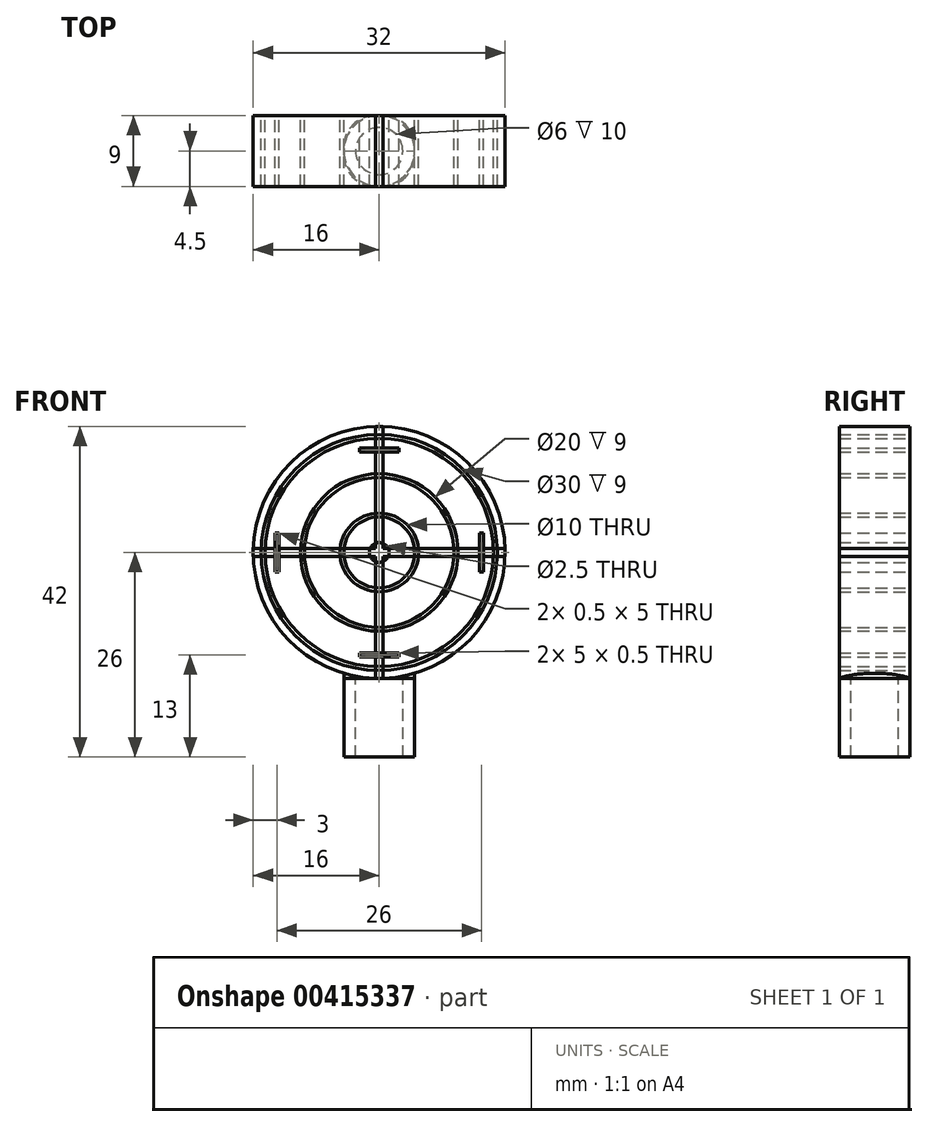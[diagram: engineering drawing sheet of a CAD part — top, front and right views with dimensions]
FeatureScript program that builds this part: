
annotation { "Feature Type Name" : "Feature", "Feature Type Description" : "" }
export const myFeature = defineFeature(function(context is Context, id is Id, definition is map)
    precondition{}
    {
        {
            var Q0;
            Q0=qCreatedBy(makeId("Top.planeOp"),FACE);
            var sketch = newSketch(context, id + "F0", { "sketchPlane" : qUnion([Q0])});
            skCircle(sketch, "E0", {"center": v(0, 0) * mm, "radius": 3 * mm});
            skCircle(sketch, "E1", {"center": v(0, 0) * mm, "radius": 4.5 * mm});
            skSolve(sketch);
        }
        {
            var Q0;
            Q0=makeQuery(id+"F0.imprint","IMPRINT",FACE,{"disambiguationData":[TD([[makeQuery(id+"F0.imprint","IMPRINT",EDGE,{"derivedFrom":sQuery(id+"F0.wireOp",EDGE,"E0")}),-1.0]])]});
            extrude(context, id + "F1", {"entities" : qUnion([Q0]), "oppositeDirection" : true, "depth" : 10 * mm});
        }
        {
            var Q0;
            Q0=qCreatedBy(makeId("Front.planeOp"),FACE);
            var sketch = newSketch(context, id + "F2", { "sketchPlane" : qUnion([Q0])});
            skLineSegment(sketch, "E2", {"start": v(0, 0) * mm, "end": v(0, 16) * mm});
            skCircle(sketch, "E3", {"center": v(0, 16) * mm, "radius": 15 * mm});
            skCircle(sketch, "E4", {"center": v(0, 16) * mm, "radius": 14.5 * mm});
            skCircle(sketch, "E5", {"center": v(0, 16) * mm, "radius": 10 * mm});
            skCircle(sketch, "E6", {"center": v(0, 16) * mm, "radius": 9.5 * mm});
            skCircle(sketch, "E7", {"center": v(0, 16) * mm, "radius": 5 * mm});
            skCircle(sketch, "E8", {"center": v(0, 16) * mm, "radius": 4.5 * mm});
            skCircle(sketch, "E9", {"center": v(0, 16) * mm, "radius": 1.25 * mm});
            skCircle(sketch, "E10", {"center": v(0, 16) * mm, "radius": 0.75 * mm});
            skCircle(sketch, "E11", {"center": v(0, 16) * mm, "radius": 16 * mm});
            skLineSegment(sketch, "E12", {"start": v(0, 0) * mm, "end": v(-4.5, 0) * mm});
            skLineSegment(sketch, "E13", {"start": v(-4.5, 0) * mm, "end": v(-4.5, 0.65) * mm});
            skLineSegment(sketch, "E14", {"start": v(0, 0) * mm, "end": v(4.5, 0) * mm});
            skLineSegment(sketch, "E15", {"start": v(4.5, 0) * mm, "end": v(4.5, 0.65) * mm});
            skSolve(sketch);
        }
        {
            var Q0;
            {var subQ0=sQuery(id+"F2.wireOp",EDGE,"E12");Q0=makeQuery(id+"F2.imprint","IMPRINT",FACE,{"disambiguationData":[TD([[makeQuery(id+"F2.imprint","IMPRINT",EDGE,{"derivedFrom":subQ0}),-1.0]])]});}
            var Q1;
            {var subQ0=sQuery(id+"F2.wireOp",EDGE,"E14");Q1=makeQuery(id+"F2.imprint","IMPRINT",FACE,{"disambiguationData":[TD([[makeQuery(id+"F2.imprint","IMPRINT",EDGE,{"derivedFrom":subQ0}),1.0]])]});}
            var Q2;
            Q2=makeQuery(id+"F2.imprint","IMPRINT",FACE,{"disambiguationData":[TD([[makeQuery(id+"F2.imprint","IMPRINT",EDGE,{"derivedFrom":sQuery(id+"F2.wireOp",EDGE,"E3")}),-1.0]])]});
            var Q3;
            Q3=makeQuery(id+"F2.imprint","IMPRINT",FACE,{"disambiguationData":[TD([[makeQuery(id+"F2.imprint","IMPRINT",EDGE,{"derivedFrom":sQuery(id+"F2.wireOp",EDGE,"E4")}),1.0]])]});
            var Q4;
            Q4=makeQuery(id+"F2.imprint","IMPRINT",FACE,{"disambiguationData":[TD([[makeQuery(id+"F2.imprint","IMPRINT",EDGE,{"derivedFrom":sQuery(id+"F2.wireOp",EDGE,"E6")}),1.0]])]});
            var Q5;
            Q5=makeQuery(id+"F2.imprint","IMPRINT",FACE,{"disambiguationData":[TD([[makeQuery(id+"F2.imprint","IMPRINT",EDGE,{"derivedFrom":sQuery(id+"F2.wireOp",EDGE,"E8")}),1.0]])]});
            extrude(context, id + "F3", {"entities" : qUnion([Q0, Q1, Q2, Q3, Q4, Q5]), "operationType" : NewBodyOperationType.ADD, "endBound" : BoundingType.SYMMETRIC, "depth" : 9 * mm});
        }
        {
            var Q0;
            Q0=makeQuery(id+"F3.opExtrude","CAP_EDGE",EDGE,{"disambiguationData":[OSD([sQuery(id+"F2.wireOp",EDGE,"E13")])],"isStart":false});
            var Q1;
            Q1=makeQuery(id+"F3.opExtrude","CAP_EDGE",EDGE,{"disambiguationData":[OSD([sQuery(id+"F2.wireOp",EDGE,"E15")])],"isStart":false});
            var Q2;
            Q2=makeQuery(id+"F3.opExtrude","CAP_EDGE",EDGE,{"disambiguationData":[OSD([sQuery(id+"F2.wireOp",EDGE,"E15")])],"isStart":true});
            var Q3;
            Q3=makeQuery(id+"F3.opExtrude","CAP_EDGE",EDGE,{"disambiguationData":[OSD([sQuery(id+"F2.wireOp",EDGE,"E13")])],"isStart":true});
            fillet(context, id + "F4", {"entities" : qUnion([Q0, Q1, Q2, Q3]), "radius" : 4 * mm, "tangentPropagation" : true, "allowEdgeOverflow" : false});
        }
        {
            var Q0;
            Q0=makeQuery(id+"F3.opExtrude","CAP_FACE",FACE,{"disambiguationData":[OSD([sQuery(id+"F2.wireOp",EDGE,"E8"),sQuery(id+"F2.wireOp",EDGE,"E9")])],"isStart":true});
            var sketch = newSketch(context, id + "F5", { "sketchPlane" : qUnion([Q0])});
            skLineSegment(sketch, "E16.bottom", {"start": v(0.5, 0) * mm, "end": v(-0.5, 0) * mm});
            skLineSegment(sketch, "E16.top", {"start": v(0.5, 32) * mm, "end": v(-0.5, 32) * mm});
            skLineSegment(sketch, "E16.left", {"start": v(0.5, 0) * mm, "end": v(0.5, 32) * mm});
            skLineSegment(sketch, "E16.right", {"start": v(-0.5, 0) * mm, "end": v(-0.5, 32) * mm});
            skPoint(sketch, "E16.middle", {"position": v(0, 16) * mm});
            skLineSegment(sketch, "E17.bottom", {"start": v(16, 15.5) * mm, "end": v(-16, 15.5) * mm});
            skLineSegment(sketch, "E17.top", {"start": v(16, 16.5) * mm, "end": v(-16, 16.5) * mm});
            skLineSegment(sketch, "E17.left", {"start": v(16, 15.5) * mm, "end": v(16, 16.5) * mm});
            skLineSegment(sketch, "E17.right", {"start": v(-16, 15.5) * mm, "end": v(-16, 16.5) * mm});
            skLineSegment(sketch, "E18", {"start": v(-16, 16) * mm, "end": v(-13, 16) * mm});
            skPoint(sketch, "E18.endSnap0", {"position": v(-16, 16) * mm});
            skLineSegment(sketch, "E19", {"start": v(0, 0) * mm, "end": v(0, 3) * mm});
            skLineSegment(sketch, "E20", {"start": v(16, 16) * mm, "end": v(13, 16) * mm});
            skLineSegment(sketch, "E21", {"start": v(0, 32) * mm, "end": v(0, 29) * mm});
            skLineSegment(sketch, "E22.bottom", {"start": v(-12.75, 13.5) * mm, "end": v(-13.25, 13.5) * mm});
            skLineSegment(sketch, "E22.top", {"start": v(-12.75, 18.5) * mm, "end": v(-13.25, 18.5) * mm});
            skLineSegment(sketch, "E22.left", {"start": v(-12.75, 13.5) * mm, "end": v(-12.75, 18.5) * mm});
            skLineSegment(sketch, "E22.right", {"start": v(-13.25, 13.5) * mm, "end": v(-13.25, 18.5) * mm});
            skPoint(sketch, "E22.middle", {"position": v(-13, 16) * mm});
            skLineSegment(sketch, "E23.bottom", {"start": v(13.25, 13.5) * mm, "end": v(12.75, 13.5) * mm});
            skLineSegment(sketch, "E23.top", {"start": v(13.25, 18.5) * mm, "end": v(12.75, 18.5) * mm});
            skLineSegment(sketch, "E23.left", {"start": v(13.25, 13.5) * mm, "end": v(13.25, 18.5) * mm});
            skLineSegment(sketch, "E23.right", {"start": v(12.75, 13.5) * mm, "end": v(12.75, 18.5) * mm});
            skPoint(sketch, "E23.middle", {"position": v(13, 16) * mm});
            skLineSegment(sketch, "E24.bottom", {"start": v(2.5, 28.75) * mm, "end": v(-2.5, 28.75) * mm});
            skLineSegment(sketch, "E24.top", {"start": v(2.5, 29.25) * mm, "end": v(-2.5, 29.25) * mm});
            skLineSegment(sketch, "E24.left", {"start": v(2.5, 28.75) * mm, "end": v(2.5, 29.25) * mm});
            skLineSegment(sketch, "E24.right", {"start": v(-2.5, 28.75) * mm, "end": v(-2.5, 29.25) * mm});
            skPoint(sketch, "E24.middle", {"position": v(0, 29) * mm});
            skLineSegment(sketch, "E25.bottom", {"start": v(2.5, 2.75) * mm, "end": v(-2.5, 2.75) * mm});
            skLineSegment(sketch, "E25.top", {"start": v(2.5, 3.25) * mm, "end": v(-2.5, 3.25) * mm});
            skLineSegment(sketch, "E25.left", {"start": v(2.5, 2.75) * mm, "end": v(2.5, 3.25) * mm});
            skLineSegment(sketch, "E25.right", {"start": v(-2.5, 2.75) * mm, "end": v(-2.5, 3.25) * mm});
            skPoint(sketch, "E25.middle", {"position": v(0, 3) * mm});
            skSolve(sketch);
        }
        {
            var Q0;
            {var subQ0=sQuery(id+"F5.wireOp",EDGE,"E24.bottom");var subQ1=sQuery(id+"F5.wireOp",EDGE,"E16.left");var subQ2=makeQuery(id+"F5.imprint","INTERSECT",VERTEX,{"derivedFrom":[subQ1,subQ0]});Q0=makeQuery(id+"F5.imprint","IMPRINT",FACE,{"disambiguationData":[TD([[makeQuery(id+"F5.imprint","IMPRINT",EDGE,{"disambiguationData":[TD([[subQ2,1.0]])],"derivedFrom":subQ1}),1.0]])]});}
            var Q1;
            {var subQ0=sQuery(id+"F5.wireOp",EDGE,"E16.right");var subQ1=sQuery(id+"F5.wireOp",EDGE,"E16.top");var subQ2=makeQuery(id+"F5.imprint","INTERSECT",VERTEX,{"derivedFrom":[subQ1,subQ0]});Q1=makeQuery(id+"F5.imprint","IMPRINT",FACE,{"disambiguationData":[TD([[makeQuery(id+"F5.imprint","IMPRINT",EDGE,{"disambiguationData":[TD([[subQ2,1.0]])],"derivedFrom":subQ1}),1.0]])]});}
            var Q2;
            {var subQ0=sQuery(id+"F5.wireOp",EDGE,"E16.left");var subQ1=sQuery(id+"F5.wireOp",EDGE,"E16.top");var subQ2=makeQuery(id+"F5.imprint","INTERSECT",VERTEX,{"derivedFrom":[subQ1,subQ0]});Q2=makeQuery(id+"F5.imprint","IMPRINT",FACE,{"disambiguationData":[TD([[makeQuery(id+"F5.imprint","IMPRINT",EDGE,{"disambiguationData":[TD([[subQ2,-1.0]])],"derivedFrom":subQ1}),1.0]])]});}
            var Q3;
            {var subQ0=sQuery(id+"F5.wireOp",EDGE,"E16.left");var subQ1=makeQuery(id+"F3.opExtrude","CAP_EDGE",EDGE,{"disambiguationData":[OSD([sQuery(id+"F2.wireOp",EDGE,"E8")])],"isStart":true});var subQ2=makeQuery(id+"F5.imprint","INTERSECT",VERTEX,{"disambiguationData":[OD(1.0)],"derivedFrom":[subQ1,subQ0]});Q3=makeQuery(id+"F5.imprint","IMPRINT",FACE,{"disambiguationData":[TD([[makeQuery(id+"F5.imprint","IMPRINT",EDGE,{"disambiguationData":[TD([[subQ2,1.0]])],"derivedFrom":subQ0}),1.0]])]});}
            var Q4;
            {var subQ0=sQuery(id+"F5.wireOp",EDGE,"E17.bottom");var subQ1=sQuery(id+"F5.wireOp",EDGE,"E16.left");var subQ2=makeQuery(id+"F5.imprint","INTERSECT",VERTEX,{"derivedFrom":[subQ1,subQ0]});Q4=makeQuery(id+"F5.imprint","IMPRINT",FACE,{"disambiguationData":[TD([[makeQuery(id+"F5.imprint","IMPRINT",EDGE,{"disambiguationData":[TD([[subQ2,-1.0]])],"derivedFrom":subQ1}),1.0]])]});}
            var Q5;
            {var subQ0=sQuery(id+"F5.wireOp",EDGE,"E17.top");var subQ1=sQuery(id+"F5.wireOp",EDGE,"E16.left");var subQ2=makeQuery(id+"F5.imprint","INTERSECT",VERTEX,{"derivedFrom":[subQ1,subQ0]});Q5=makeQuery(id+"F5.imprint","IMPRINT",FACE,{"disambiguationData":[TD([[makeQuery(id+"F5.imprint","IMPRINT",EDGE,{"disambiguationData":[TD([[subQ2,-1.0]])],"derivedFrom":subQ1}),1.0]])]});}
            var Q6;
            {var subQ0=sQuery(id+"F5.wireOp",EDGE,"E16.left");var subQ1=makeQuery(id+"F3.opExtrude","CAP_EDGE",EDGE,{"disambiguationData":[OSD([sQuery(id+"F2.wireOp",EDGE,"E8")])],"isStart":true});var subQ2=makeQuery(id+"F5.imprint","INTERSECT",VERTEX,{"disambiguationData":[OD(0.0)],"derivedFrom":[subQ1,subQ0]});Q6=makeQuery(id+"F5.imprint","IMPRINT",FACE,{"disambiguationData":[TD([[makeQuery(id+"F5.imprint","IMPRINT",EDGE,{"disambiguationData":[TD([[subQ2,-1.0]])],"derivedFrom":subQ0}),1.0]])]});}
            var Q7;
            {var subQ0=sQuery(id+"F5.wireOp",EDGE,"E17.bottom");var subQ1=sQuery(id+"F5.wireOp",EDGE,"E16.left");var subQ2=makeQuery(id+"F5.imprint","INTERSECT",VERTEX,{"derivedFrom":[subQ1,subQ0]});Q7=makeQuery(id+"F5.imprint","IMPRINT",FACE,{"disambiguationData":[TD([[makeQuery(id+"F5.imprint","IMPRINT",EDGE,{"disambiguationData":[TD([[subQ2,1.0]])],"derivedFrom":subQ1}),1.0]])]});}
            var Q8;
            {var subQ0=sQuery(id+"F5.wireOp",EDGE,"E25.top");var subQ1=sQuery(id+"F5.wireOp",EDGE,"E16.left");var subQ2=makeQuery(id+"F5.imprint","INTERSECT",VERTEX,{"derivedFrom":[subQ1,subQ0]});Q8=makeQuery(id+"F5.imprint","IMPRINT",FACE,{"disambiguationData":[TD([[makeQuery(id+"F5.imprint","IMPRINT",EDGE,{"disambiguationData":[TD([[subQ2,-1.0]])],"derivedFrom":subQ1}),1.0]])]});}
            var Q9;
            {var subQ0=sQuery(id+"F5.wireOp",EDGE,"E16.right");var subQ1=sQuery(id+"F5.wireOp",EDGE,"E16.bottom");var subQ2=makeQuery(id+"F5.imprint","INTERSECT",VERTEX,{"derivedFrom":[subQ1,subQ0]});Q9=makeQuery(id+"F5.imprint","IMPRINT",FACE,{"disambiguationData":[TD([[makeQuery(id+"F5.imprint","IMPRINT",EDGE,{"disambiguationData":[TD([[subQ2,1.0]])],"derivedFrom":subQ1}),-1.0]])]});}
            var Q10;
            {var subQ0=sQuery(id+"F5.wireOp",EDGE,"E16.left");var subQ1=sQuery(id+"F5.wireOp",EDGE,"E16.bottom");var subQ2=makeQuery(id+"F5.imprint","INTERSECT",VERTEX,{"derivedFrom":[subQ1,subQ0]});Q10=makeQuery(id+"F5.imprint","IMPRINT",FACE,{"disambiguationData":[TD([[makeQuery(id+"F5.imprint","IMPRINT",EDGE,{"disambiguationData":[TD([[subQ2,-1.0]])],"derivedFrom":subQ1}),-1.0]])]});}
            var Q11;
            {var subQ0=sQuery(id+"F5.wireOp",EDGE,"E17.right");var subQ1=sQuery(id+"F5.wireOp",EDGE,"E17.top");var subQ2=makeQuery(id+"F5.imprint","INTERSECT",VERTEX,{"derivedFrom":[subQ1,subQ0]});Q11=makeQuery(id+"F5.imprint","IMPRINT",FACE,{"disambiguationData":[TD([[makeQuery(id+"F5.imprint","IMPRINT",EDGE,{"disambiguationData":[TD([[subQ2,1.0]])],"derivedFrom":subQ1}),1.0]])]});}
            var Q12;
            {var subQ0=sQuery(id+"F5.wireOp",EDGE,"E17.right");var subQ1=sQuery(id+"F5.wireOp",EDGE,"E17.bottom");var subQ2=makeQuery(id+"F5.imprint","INTERSECT",VERTEX,{"derivedFrom":[subQ1,subQ0]});Q12=makeQuery(id+"F5.imprint","IMPRINT",FACE,{"disambiguationData":[TD([[makeQuery(id+"F5.imprint","IMPRINT",EDGE,{"disambiguationData":[TD([[subQ2,1.0]])],"derivedFrom":subQ1}),-1.0]])]});}
            var Q13;
            {var subQ0=sQuery(id+"F5.wireOp",EDGE,"E22.left");var subQ1=sQuery(id+"F5.wireOp",EDGE,"E17.bottom");var subQ2=makeQuery(id+"F5.imprint","INTERSECT",VERTEX,{"derivedFrom":[subQ1,subQ0]});Q13=makeQuery(id+"F5.imprint","IMPRINT",FACE,{"disambiguationData":[TD([[makeQuery(id+"F5.imprint","IMPRINT",EDGE,{"disambiguationData":[TD([[subQ2,1.0]])],"derivedFrom":subQ1}),-1.0]])]});}
            var Q14;
            {var subQ0=sQuery(id+"F5.wireOp",EDGE,"E17.bottom");var subQ1=makeQuery(id+"F3.opExtrude","CAP_EDGE",EDGE,{"disambiguationData":[OSD([sQuery(id+"F2.wireOp",EDGE,"E8")])],"isStart":true});var subQ2=makeQuery(id+"F5.imprint","INTERSECT",VERTEX,{"disambiguationData":[OD(1.0)],"derivedFrom":[subQ1,subQ0]});Q14=makeQuery(id+"F5.imprint","IMPRINT",FACE,{"disambiguationData":[TD([[makeQuery(id+"F5.imprint","IMPRINT",EDGE,{"disambiguationData":[TD([[subQ2,1.0]])],"derivedFrom":subQ0}),-1.0]])]});}
            var Q15;
            {var subQ0=sQuery(id+"F5.wireOp",EDGE,"E17.bottom");var subQ1=sQuery(id+"F5.wireOp",EDGE,"E16.right");var subQ2=makeQuery(id+"F5.imprint","INTERSECT",VERTEX,{"derivedFrom":[subQ1,subQ0]});Q15=makeQuery(id+"F5.imprint","IMPRINT",FACE,{"disambiguationData":[TD([[makeQuery(id+"F5.imprint","IMPRINT",EDGE,{"disambiguationData":[TD([[subQ2,-1.0]])],"derivedFrom":subQ1}),1.0]])]});}
            var Q16;
            {var subQ0=sQuery(id+"F5.wireOp",EDGE,"E17.bottom");var subQ1=makeQuery(id+"F3.opExtrude","CAP_EDGE",EDGE,{"disambiguationData":[OSD([sQuery(id+"F2.wireOp",EDGE,"E8")])],"isStart":true});var subQ2=makeQuery(id+"F5.imprint","INTERSECT",VERTEX,{"disambiguationData":[OD(0.0)],"derivedFrom":[subQ1,subQ0]});Q16=makeQuery(id+"F5.imprint","IMPRINT",FACE,{"disambiguationData":[TD([[makeQuery(id+"F5.imprint","IMPRINT",EDGE,{"disambiguationData":[TD([[subQ2,-1.0]])],"derivedFrom":subQ0}),-1.0]])]});}
            var Q17;
            {var subQ0=sQuery(id+"F5.wireOp",EDGE,"E17.bottom");var subQ1=sQuery(id+"F5.wireOp",EDGE,"E16.left");var subQ2=makeQuery(id+"F5.imprint","INTERSECT",VERTEX,{"derivedFrom":[subQ1,subQ0]});Q17=makeQuery(id+"F5.imprint","IMPRINT",FACE,{"disambiguationData":[TD([[makeQuery(id+"F5.imprint","IMPRINT",EDGE,{"disambiguationData":[TD([[subQ2,-1.0]])],"derivedFrom":subQ1}),-1.0]])]});}
            var Q18;
            {var subQ0=sQuery(id+"F5.wireOp",EDGE,"E23.right");var subQ1=sQuery(id+"F5.wireOp",EDGE,"E17.bottom");var subQ2=makeQuery(id+"F5.imprint","INTERSECT",VERTEX,{"derivedFrom":[subQ1,subQ0]});Q18=makeQuery(id+"F5.imprint","IMPRINT",FACE,{"disambiguationData":[TD([[makeQuery(id+"F5.imprint","IMPRINT",EDGE,{"disambiguationData":[TD([[subQ2,-1.0]])],"derivedFrom":subQ1}),-1.0]])]});}
            var Q19;
            {var subQ0=sQuery(id+"F5.wireOp",EDGE,"E17.left");var subQ1=sQuery(id+"F5.wireOp",EDGE,"E17.bottom");var subQ2=makeQuery(id+"F5.imprint","INTERSECT",VERTEX,{"derivedFrom":[subQ1,subQ0]});Q19=makeQuery(id+"F5.imprint","IMPRINT",FACE,{"disambiguationData":[TD([[makeQuery(id+"F5.imprint","IMPRINT",EDGE,{"disambiguationData":[TD([[subQ2,-1.0]])],"derivedFrom":subQ1}),-1.0]])]});}
            var Q20;
            {var subQ0=sQuery(id+"F5.wireOp",EDGE,"E17.left");var subQ1=sQuery(id+"F5.wireOp",EDGE,"E17.top");var subQ2=makeQuery(id+"F5.imprint","INTERSECT",VERTEX,{"derivedFrom":[subQ1,subQ0]});Q20=makeQuery(id+"F5.imprint","IMPRINT",FACE,{"disambiguationData":[TD([[makeQuery(id+"F5.imprint","IMPRINT",EDGE,{"disambiguationData":[TD([[subQ2,-1.0]])],"derivedFrom":subQ1}),1.0]])]});}
            extrude(context, id + "F6", {"entities" : qUnion([Q0, Q1, Q2, Q3, Q4, Q5, Q6, Q7, Q8, Q9, Q10, Q11, Q12, Q13, Q14, Q15, Q16, Q17, Q18, Q19, Q20]), "oppositeDirection" : true, "depth" : 9 * mm});
        }
        {
            var Q0;
            {var subQ5=sQuery(id+"F5.wireOp",EDGE,"E22.top");Q0=makeQuery(id+"F5.imprint","IMPRINT",FACE,{"disambiguationData":[TD([[makeQuery(id+"F5.imprint","IMPRINT",EDGE,{"derivedFrom":subQ5}),1.0]])]});}
            var Q1;
            {var subQ1=sQuery(id+"F5.wireOp",EDGE,"E17.bottom");var subQ4=sQuery(id+"F5.wireOp",EDGE,"E22.left");var subQ5=makeQuery(id+"F5.imprint","INTERSECT",VERTEX,{"derivedFrom":[subQ1,subQ4]});Q1=makeQuery(id+"F5.imprint","IMPRINT",FACE,{"disambiguationData":[TD([[makeQuery(id+"F5.imprint","IMPRINT",EDGE,{"disambiguationData":[TD([[subQ5,-1.0]])],"derivedFrom":subQ1}),-1.0]])]});}
            var Q2;
            {var subQ5=sQuery(id+"F5.wireOp",EDGE,"E22.bottom");Q2=makeQuery(id+"F5.imprint","IMPRINT",FACE,{"disambiguationData":[TD([[makeQuery(id+"F5.imprint","IMPRINT",EDGE,{"derivedFrom":subQ5}),-1.0]])]});}
            var Q3;
            {var subQ5=sQuery(id+"F5.wireOp",EDGE,"E25.right");Q3=makeQuery(id+"F5.imprint","IMPRINT",FACE,{"disambiguationData":[TD([[makeQuery(id+"F5.imprint","IMPRINT",EDGE,{"derivedFrom":subQ5}),-1.0]])]});}
            var Q4;
            {var subQ0=sQuery(id+"F5.wireOp",EDGE,"E25.bottom");var subQ1=sQuery(id+"F5.wireOp",EDGE,"E16.left");var subQ2=makeQuery(id+"F5.imprint","INTERSECT",VERTEX,{"derivedFrom":[subQ1,subQ0]});Q4=makeQuery(id+"F5.imprint","IMPRINT",FACE,{"disambiguationData":[TD([[makeQuery(id+"F5.imprint","IMPRINT",EDGE,{"disambiguationData":[TD([[subQ2,-1.0]])],"derivedFrom":subQ1}),1.0]])]});}
            var Q5;
            {var subQ5=sQuery(id+"F5.wireOp",EDGE,"E25.left");Q5=makeQuery(id+"F5.imprint","IMPRINT",FACE,{"disambiguationData":[TD([[makeQuery(id+"F5.imprint","IMPRINT",EDGE,{"derivedFrom":subQ5}),1.0]])]});}
            var Q6;
            {var subQ5=sQuery(id+"F5.wireOp",EDGE,"E23.bottom");Q6=makeQuery(id+"F5.imprint","IMPRINT",FACE,{"disambiguationData":[TD([[makeQuery(id+"F5.imprint","IMPRINT",EDGE,{"derivedFrom":subQ5}),-1.0]])]});}
            var Q7;
            {var subQ0=sQuery(id+"F5.wireOp",EDGE,"E23.left");var subQ4=sQuery(id+"F5.wireOp",EDGE,"E17.bottom");var subQ5=makeQuery(id+"F5.imprint","INTERSECT",VERTEX,{"derivedFrom":[subQ4,subQ0]});Q7=makeQuery(id+"F5.imprint","IMPRINT",FACE,{"disambiguationData":[TD([[makeQuery(id+"F5.imprint","IMPRINT",EDGE,{"disambiguationData":[TD([[subQ5,-1.0]])],"derivedFrom":subQ4}),-1.0]])]});}
            var Q8;
            {var subQ5=sQuery(id+"F5.wireOp",EDGE,"E23.top");Q8=makeQuery(id+"F5.imprint","IMPRINT",FACE,{"disambiguationData":[TD([[makeQuery(id+"F5.imprint","IMPRINT",EDGE,{"derivedFrom":subQ5}),1.0]])]});}
            var Q9;
            {var subQ5=sQuery(id+"F5.wireOp",EDGE,"E24.right");Q9=makeQuery(id+"F5.imprint","IMPRINT",FACE,{"disambiguationData":[TD([[makeQuery(id+"F5.imprint","IMPRINT",EDGE,{"derivedFrom":subQ5}),-1.0]])]});}
            var Q10;
            {var subQ0=sQuery(id+"F5.wireOp",EDGE,"E24.bottom");var subQ1=sQuery(id+"F5.wireOp",EDGE,"E16.left");var subQ2=makeQuery(id+"F5.imprint","INTERSECT",VERTEX,{"derivedFrom":[subQ1,subQ0]});Q10=makeQuery(id+"F5.imprint","IMPRINT",FACE,{"disambiguationData":[TD([[makeQuery(id+"F5.imprint","IMPRINT",EDGE,{"disambiguationData":[TD([[subQ2,-1.0]])],"derivedFrom":subQ1}),1.0]])]});}
            var Q11;
            {var subQ5=sQuery(id+"F5.wireOp",EDGE,"E24.left");Q11=makeQuery(id+"F5.imprint","IMPRINT",FACE,{"disambiguationData":[TD([[makeQuery(id+"F5.imprint","IMPRINT",EDGE,{"derivedFrom":subQ5}),1.0]])]});}
            extrude(context, id + "F7", {"entities" : qUnion([Q0, Q1, Q2, Q3, Q4, Q5, Q6, Q7, Q8, Q9, Q10, Q11]), "operationType" : NewBodyOperationType.REMOVE, "oppositeDirection" : true, "depth" : 25 * mm});
        }
    });
